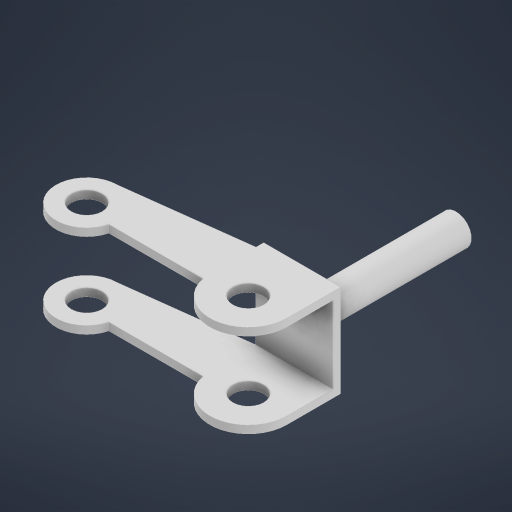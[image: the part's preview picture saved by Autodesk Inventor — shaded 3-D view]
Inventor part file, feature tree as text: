
AUTODESK INVENTOR PART (.ipt)
format: ipt  version: 2023.2 (Build 272271000, 271)  size: 352,256 bytes
history: native  units: mm
features: sketch x2
ambient origin geometry x8: Origin, YZ Plane, XZ Plane, XY Plane, X Axis, Y Axis, Z Axis, Center Point
bodies: Body1 (feature_tree)
feature tree (2):
  sketch  "Sketch2"  dims[d235=1.0mm d236=0.0mm]
  sketch  "Sketch4"  dims[d238=10.0mm d239=0.0mm d245=1.0mm d246=0.0mm d269=4.0mm d270=12.0mm d271=1.0mm d272=4.0mm d273=4.0mm d274=-1.0mm d275=-1.0mm d278=7.0mm d279=10.0mm d280=5.0mm d282=4.0mm d284=5.0mm d286=5.0mm d287=4.0mm d288=1.0mm d291=4.0mm d294=4.0mm d295=4.0mm d296=4.0mm d297=6.0mm d298=5.0mm d299=20.0mm d300=0.0mm d9=0.5mm d10=0.872665mm d11=0.5mm d12=0.872665mm d13=0.5mm d14=0.872665mm d27=0.5mm d28=0.872665mm d29=0.5mm d30=0.872665mm d88=0.5mm d89=0.872665mm d90=0.5mm d91=0.872665mm d116=0.5mm d117=0.872665mm d118=0.5mm d119=0.872665mm d154=0.5mm d155=0.872665mm d156=0.5mm d157=0.872665mm d181=0.5mm d182=0.872665mm d183=0.5mm d184=0.872665mm d221=0.5mm d222=0.872665mm d223=0.5mm d224=0.872665mm]
